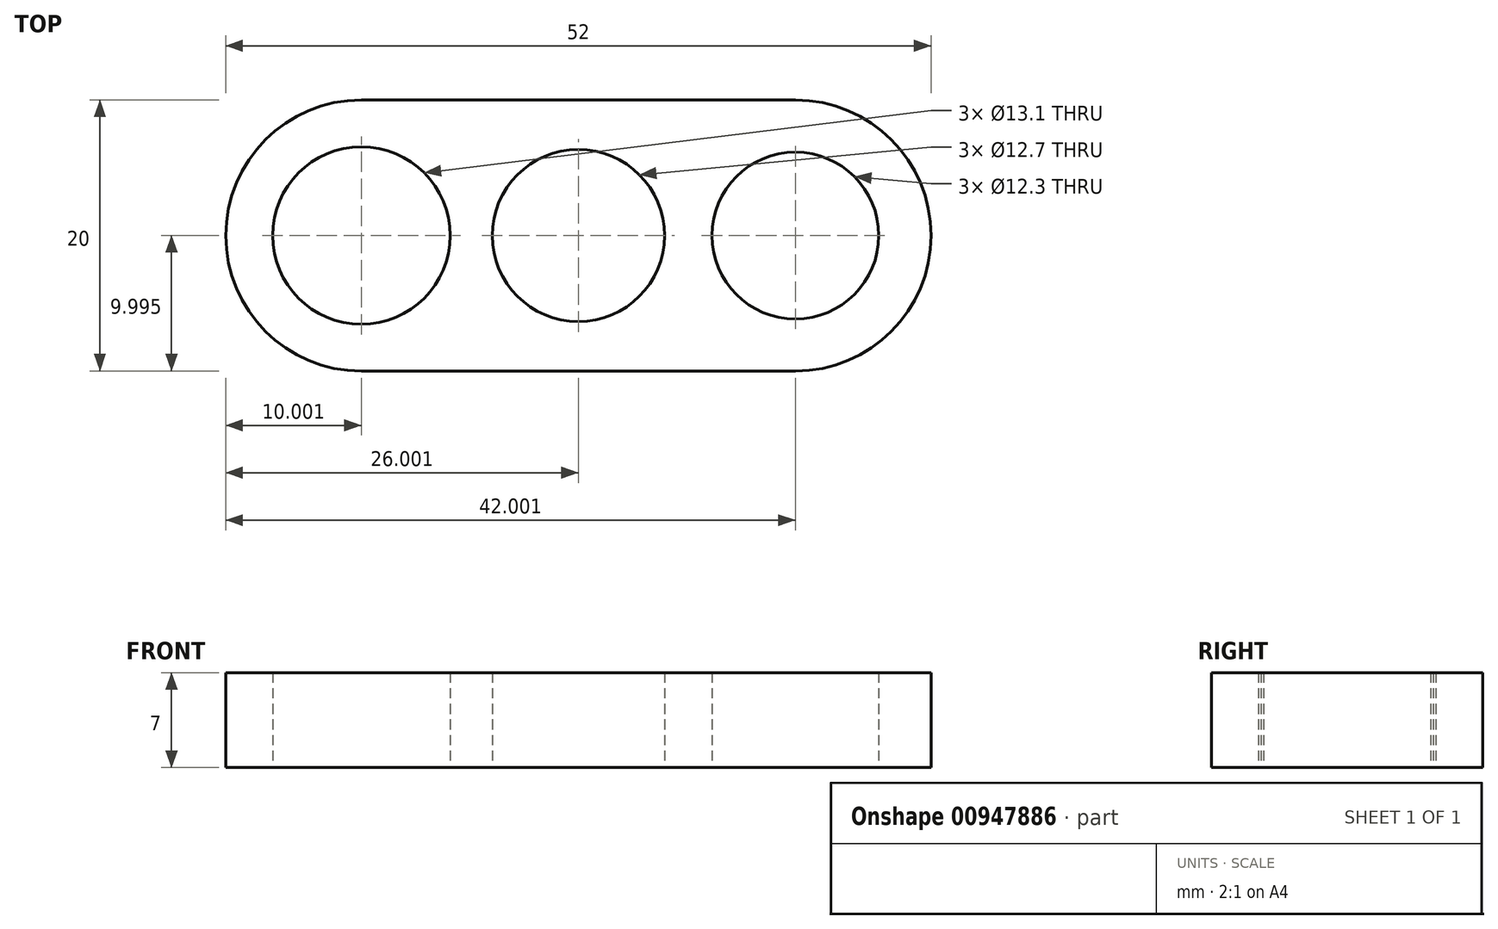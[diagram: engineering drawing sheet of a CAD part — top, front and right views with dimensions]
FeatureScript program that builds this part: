
annotation { "Feature Type Name" : "Feature", "Feature Type Description" : "" }
export const myFeature = defineFeature(function(context is Context, id is Id, definition is map)
    precondition{}
    {
        {
            var Q0;
            Q0=qCreatedBy(makeId("Top.planeOp"),FACE);
            var sketch = newSketch(context, id + "F0", { "sketchPlane" : qUnion([Q0])});
            skLineSegment(sketch, "E0", {"start": v(-32.79, 5.8) * mm, "end": v(-0.79, 5.8) * mm, "construction": true});
            skCircle(sketch, "E1", {"center": v(-32.79, 5.8) * mm, "radius": 6.55 * mm});
            skCircle(sketch, "E2", {"center": v(-16.79, 5.8) * mm, "radius": 6.35 * mm});
            skCircle(sketch, "E3", {"center": v(-0.79, 5.8) * mm, "radius": 6.15 * mm});
            skCircle(sketch, "E4", {"center": v(-32.79, 5.8) * mm, "radius": 10 * mm});
            skCircle(sketch, "E5", {"center": v(-0.79, 5.8) * mm, "radius": 10 * mm});
            skLineSegment(sketch, "E6", {"start": v(-32.79, -4.2) * mm, "end": v(-0.79, -4.2) * mm});
            skLineSegment(sketch, "E7", {"start": v(-32.79, 15.8) * mm, "end": v(-0.79, 15.8) * mm});
            skSolve(sketch);
        }
        {
            var Q0;
            Q0=makeQuery(id+"F0.imprint","IMPRINT",FACE,{"disambiguationData":[TD([[makeQuery(id+"F0.imprint","IMPRINT",EDGE,{"derivedFrom":sQuery(id+"F0.wireOp",EDGE,"E1")}),-1.0]])]});
            var Q1;
            {var subQ5=sQuery(id+"F0.wireOp",EDGE,"E6");Q1=makeQuery(id+"F0.imprint","IMPRINT",FACE,{"disambiguationData":[TD([[makeQuery(id+"F0.imprint","IMPRINT",EDGE,{"derivedFrom":subQ5}),1.0]])]});}
            var Q2;
            {var subQ5=sQuery(id+"F0.wireOp",EDGE,"E7");Q2=makeQuery(id+"F0.imprint","IMPRINT",FACE,{"disambiguationData":[TD([[makeQuery(id+"F0.imprint","IMPRINT",EDGE,{"derivedFrom":subQ5}),-1.0]])]});}
            var Q3;
            Q3=makeQuery(id+"F0.imprint","IMPRINT",FACE,{"disambiguationData":[TD([[makeQuery(id+"F0.imprint","IMPRINT",EDGE,{"derivedFrom":sQuery(id+"F0.wireOp",EDGE,"E3")}),-1.0]])]});
            extrude(context, id + "F1", {"entities" : qUnion([Q0, Q1, Q2, Q3]), "depth" : 7 * mm, "offsetDistance" : 25 * mm});
        }
    });
